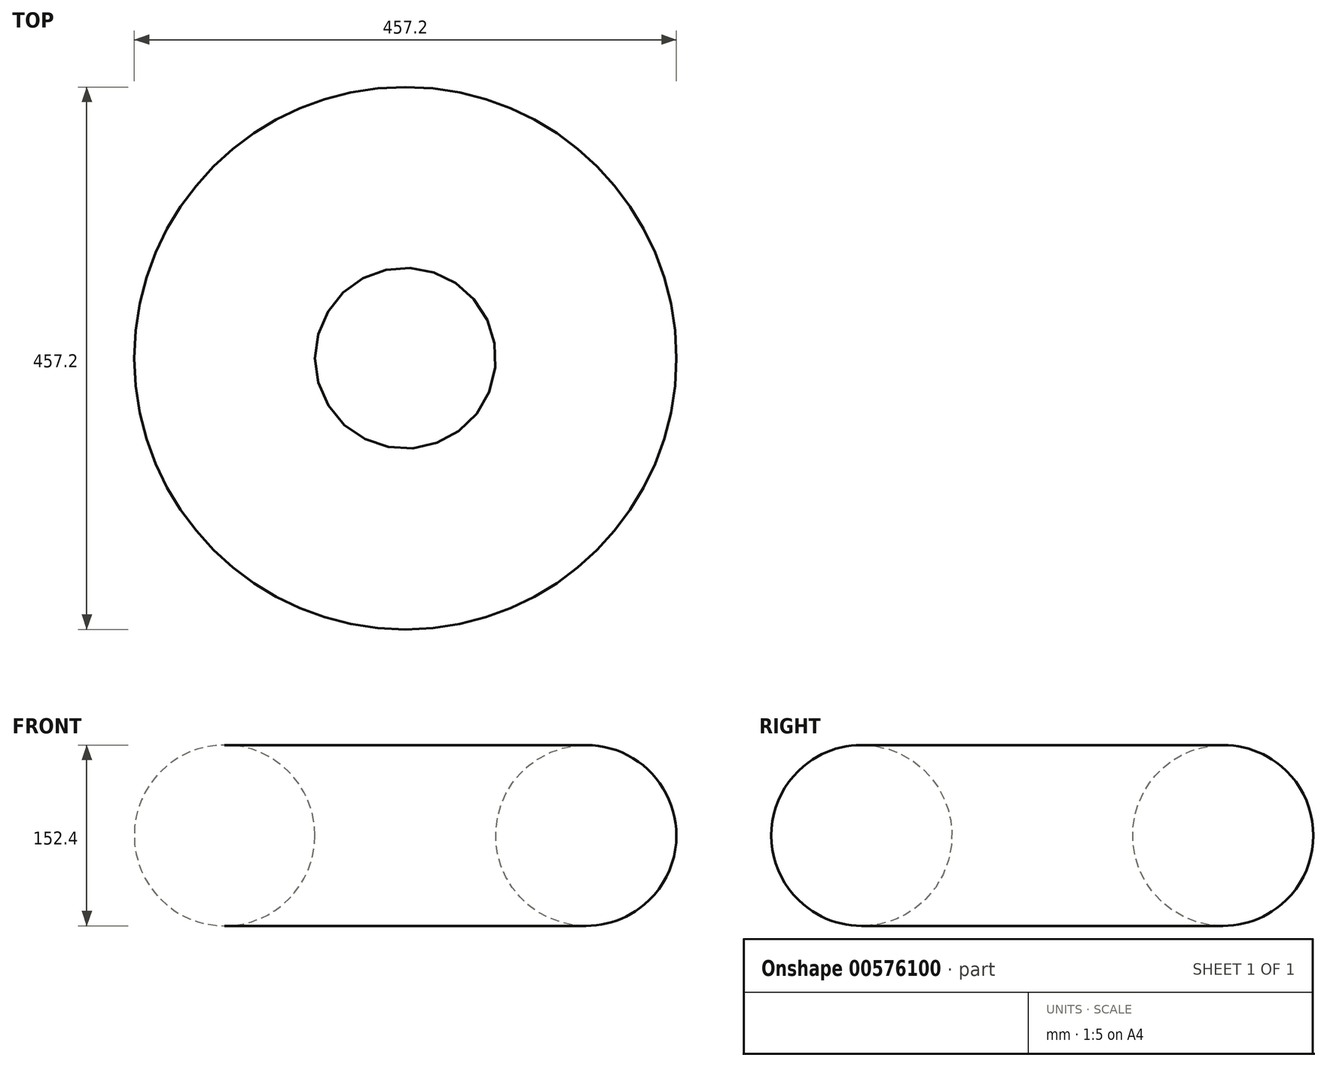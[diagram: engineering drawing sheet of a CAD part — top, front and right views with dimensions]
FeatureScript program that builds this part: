
annotation { "Feature Type Name" : "Feature", "Feature Type Description" : "" }
export const myFeature = defineFeature(function(context is Context, id is Id, definition is map)
    precondition{}
    {
        {
            var Q0;
            Q0=qCreatedBy(makeId("Front.planeOp"),FACE);
            var sketch = newSketch(context, id + "F0", { "sketchPlane" : qUnion([Q0])});
            skLineSegment(sketch, "E0.bottom", {"start": v(-0.5, 145.89) * mm, "end": v(-0.5, 145.89) * mm});
            skLineSegment(sketch, "E0.top", {"start": v(-0.5, -6.51) * mm, "end": v(-0.5, -6.51) * mm});
            skLineSegment(sketch, "E0.left", {"start": v(-76.7, 69.69) * mm, "end": v(-76.7, 69.69) * mm});
            skLineSegment(sketch, "E0.right", {"start": v(75.7, 69.69) * mm, "end": v(75.7, 69.69) * mm});
            skPoint(sketch, "E1.visualSharp", {"position": v(-76.7, 145.89) * mm});
            skArc(sketch, "E1.filletArc", {"start": v(-0.5, 145.89) * mm, "mid": v(-54.38, 123.57) * mm, "end": v(-76.7, 69.69) * mm});
            skPoint(sketch, "E2.visualSharp", {"position": v(75.7, 145.89) * mm});
            skArc(sketch, "E2.filletArc", {"start": v(75.7, 69.69) * mm, "mid": v(53.38, 123.57) * mm, "end": v(-0.5, 145.89) * mm});
            skPoint(sketch, "E3.visualSharp", {"position": v(75.7, -6.51) * mm});
            skArc(sketch, "E3.filletArc", {"start": v(-0.5, -6.51) * mm, "mid": v(53.38, 15.8) * mm, "end": v(75.7, 69.69) * mm});
            skPoint(sketch, "E4.visualSharp", {"position": v(-76.7, -6.51) * mm});
            skArc(sketch, "E4.filletArc", {"start": v(-76.7, 69.69) * mm, "mid": v(-54.38, 15.8) * mm, "end": v(-0.5, -6.51) * mm});
            skLineSegment(sketch, "E5", {"start": v(-76.7, 69.69) * mm, "end": v(-152.9, 69.69) * mm});
            skLineSegment(sketch, "E6", {"start": v(-152.9, 69.69) * mm, "end": v(-152.9, 97.7) * mm});
            skSolve(sketch);
        }
        {
            var Q0;
            Q0=makeQuery(id+"F0.imprint","IMPRINT",FACE,{"disambiguationData":[TD([[makeQuery(id+"F0.imprint","IMPRINT",EDGE,{"derivedFrom":sQuery(id+"F0.wireOp",EDGE,"E1.filletArc")}),1.0]])]});
            var Q1;
            Q1=sQuery(id+"F0.wireOp",EDGE,"E6");
            revolve(context, id + "F1", {"entities" : qUnion([Q0]), "axis" : qUnion([Q1]), "revolveType" : RevolveType.FULL});
        }
    });
